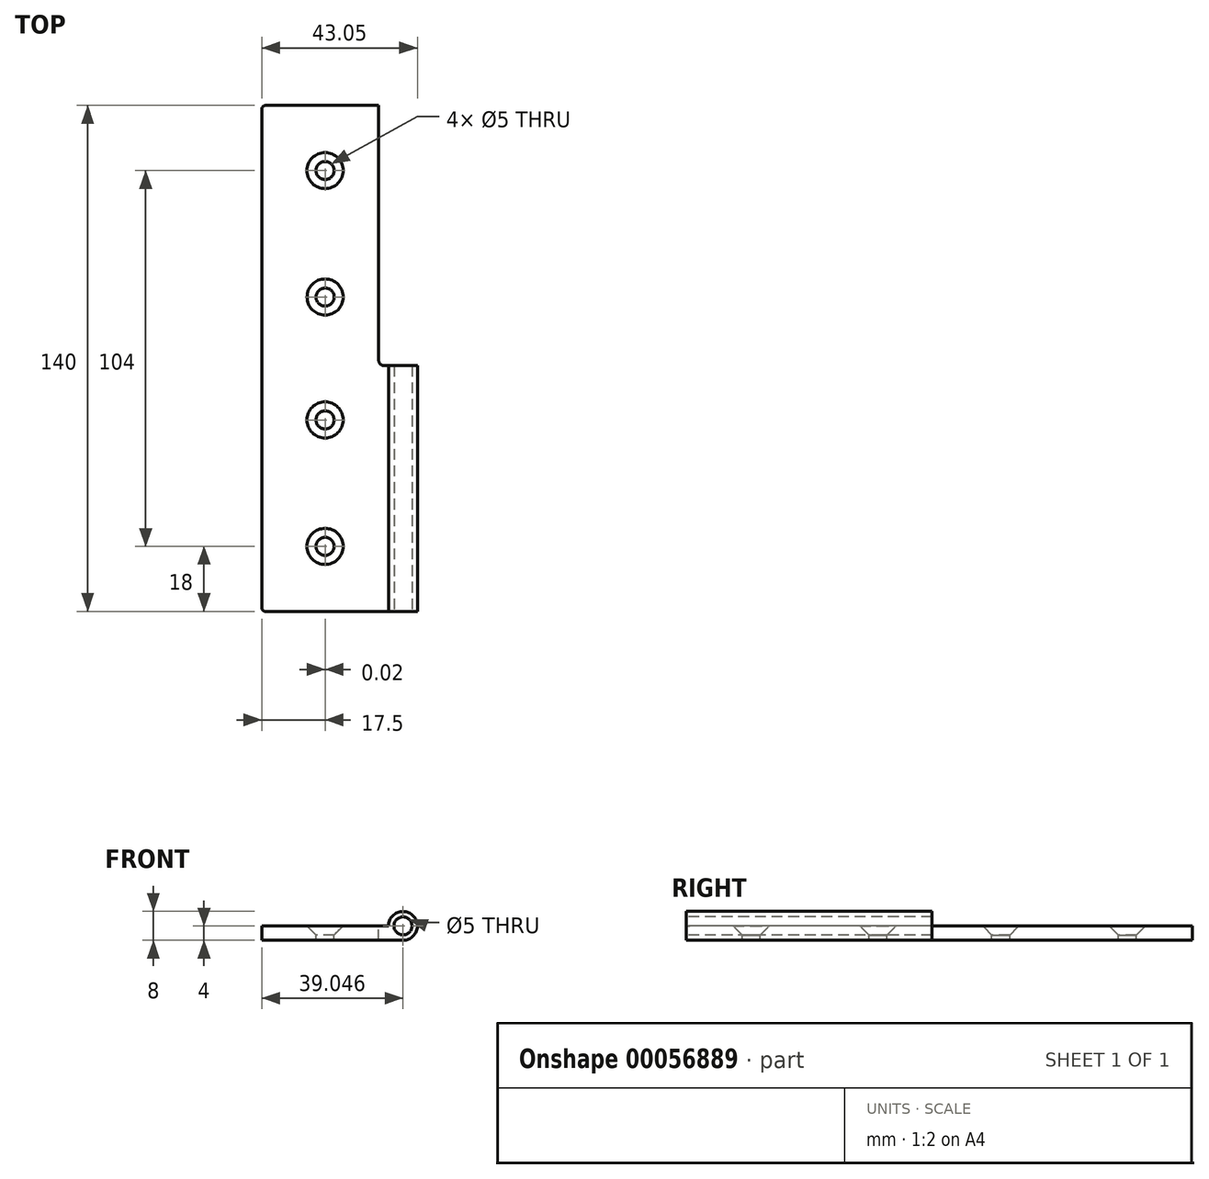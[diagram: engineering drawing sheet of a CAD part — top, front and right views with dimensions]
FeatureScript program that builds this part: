
annotation { "Feature Type Name" : "Feature", "Feature Type Description" : "" }
export const myFeature = defineFeature(function(context is Context, id is Id, definition is map)
    precondition{}
    {
        {
            var Q0;
            Q0=qCreatedBy(makeId("Top.planeOp"),FACE);
            var sketch = newSketch(context, id + "F0", { "sketchPlane" : qUnion([Q0])});
            skLineSegment(sketch, "E0.bottom", {"start": v(-17.5, 70) * mm, "end": v(17.5, 70) * mm});
            skLineSegment(sketch, "E0.top", {"start": v(-17.5, -70) * mm, "end": v(17.5, -70) * mm});
            skLineSegment(sketch, "E0.left", {"start": v(-17.5, 70) * mm, "end": v(-17.5, -70) * mm});
            skLineSegment(sketch, "E0.right", {"start": v(17.5, 70) * mm, "end": v(17.5, -70) * mm});
            skSolve(sketch);
        }
        {
            var Q0;
            Q0=makeQuery(id+"F0.imprint","IMPRINT",FACE,{"disambiguationData":[TD([[makeQuery(id+"F0.imprint","IMPRINT",EDGE,{"derivedFrom":sQuery(id+"F0.wireOp",EDGE,"E0.bottom")}),-1.0]])]});
            extrude(context, id + "F1", {"entities" : qUnion([Q0]), "depth" : 4 * mm});
        }
        {
            var Q0;
            Q0=makeQuery(id+"F1.opExtrude","SWEPT_FACE",FACE,{"disambiguationData":[OSD([sQuery(id+"F0.wireOp",EDGE,"E0.top")])]});
            var sketch = newSketch(context, id + "F2", { "sketchPlane" : qUnion([Q0])});
            skLineSegment(sketch, "E1", {"start": v(17.5, 0) * mm, "end": v(21.55, 0) * mm});
            skArc(sketch, "E2", {"start": v(21.55, 0) * mm, "mid": v(24.37, 6.83) * mm, "end": v(17.55, 4) * mm});
            skCircle(sketch, "E3", {"center": v(21.55, 4) * mm, "radius": 2.5 * mm});
            skLineSegment(sketch, "E4", {"start": v(17.5, 4) * mm, "end": v(17.55, 4) * mm});
            skSolve(sketch);
        }
        {
            var Q0;
            Q0=makeQuery(id+"F2.imprint","IMPRINT",FACE,{"disambiguationData":[TD([[makeQuery(id+"F2.imprint","IMPRINT",EDGE,{"derivedFrom":sQuery(id+"F2.wireOp",EDGE,"E2")}),1.0]])]});
            extrude(context, id + "F3", {"entities" : qUnion([Q0]), "oppositeDirection" : true, "depth" : 68 * mm});
        }
        {
            var Q0;
            Q0=makeQuery(id+"F3.opExtrude","SWEPT_BODY",BODY,{"disambiguationData":[OSD([sQuery(id+"F2.wireOp",EDGE,"E2"),sQuery(id+"F2.wireOp",EDGE,"E3")])]});
            var Q1;
            Q1=makeQuery(id+"F1.opExtrude","SWEPT_BODY",BODY,{"disambiguationData":[OSD([sQuery(id+"F0.wireOp",EDGE,"E0.bottom"),sQuery(id+"F0.wireOp",EDGE,"E0.top"),sQuery(id+"F0.wireOp",EDGE,"E0.left"),sQuery(id+"F0.wireOp",EDGE,"E0.right")])]});
            booleanBodies(context, id + "F4", {"operationType" : BooleanOperationType.UNION, "tools" : qUnion([Q0, Q1])});
        }
        {
            var Q0;
            Q0=makeQuery(id+"F4.opBoolean","MERGE",FACE,{"derivedFrom":[makeQuery(id+"F1.opExtrude","CAP_FACE",FACE,{"disambiguationData":[OSD([sQuery(id+"F0.wireOp",EDGE,"E0.bottom"),sQuery(id+"F0.wireOp",EDGE,"E0.top"),sQuery(id+"F0.wireOp",EDGE,"E0.left"),sQuery(id+"F0.wireOp",EDGE,"E0.right")])],"isStart":false}),makeQuery(id+"F3.opExtrude","SWEPT_FACE",FACE,{"disambiguationData":[OSD([sQuery(id+"F2.wireOp",EDGE,"E4")])]})]});
            var sketch = newSketch(context, id + "F5", { "sketchPlane" : qUnion([Q0])});
            skPoint(sketch, "E5", {"position": v(0, -52) * mm});
            skPoint(sketch, "E6", {"position": v(0, -17) * mm});
            skPoint(sketch, "E7", {"position": v(0.02, 17) * mm});
            skPoint(sketch, "E8", {"position": v(0, 52) * mm});
            skSolve(sketch);
        }
        {
            var Q0;
            Q0=sQuery(id+"F5.wireOp",VERTEX,"E5");
            var Q1;
            Q1=sQuery(id+"F5.wireOp",VERTEX,"E6");
            var Q2;
            Q2=sQuery(id+"F5.wireOp",VERTEX,"E7");
            var Q3;
            Q3=sQuery(id+"F5.wireOp",VERTEX,"E8");
            var Q4;
            Q4=makeQuery(id+"F3.opExtrude","SWEPT_BODY",BODY,{"disambiguationData":[OSD([sQuery(id+"F0.wireOp",EDGE,"E0.top"),sQuery(id+"F0.wireOp",EDGE,"E0.right"),sQuery(id+"F2.wireOp",EDGE,"E1"),sQuery(id+"F2.wireOp",EDGE,"E2"),sQuery(id+"F2.wireOp",EDGE,"E3"),sQuery(id+"F2.wireOp",EDGE,"E4")])]});
            hole(context, id + "F6", {"style" : HoleStyle.C_SINK, "holeDiameter" : 5 * mm, "cSinkDiameter" : 10 * mm, "endStyle" : HoleEndStyle.THROUGH, "locations" : qUnion([Q0, Q1, Q2, Q3]), "scope" : qUnion([Q4]), "cSinkAngle" : 90 * degree});
        }
        {
            var Q0;
            Q0=makeQuery(id+"F4.opBoolean","MERGE",FACE,{"derivedFrom":[makeQuery(id+"F1.opExtrude","CAP_FACE",FACE,{"disambiguationData":[OSD([sQuery(id+"F0.wireOp",EDGE,"E0.bottom"),sQuery(id+"F0.wireOp",EDGE,"E0.top"),sQuery(id+"F0.wireOp",EDGE,"E0.left"),sQuery(id+"F0.wireOp",EDGE,"E0.right")])],"isStart":false}),makeQuery(id+"F3.opExtrude","SWEPT_FACE",FACE,{"disambiguationData":[OSD([sQuery(id+"F2.wireOp",EDGE,"E4")])]})]});
            var sketch = newSketch(context, id + "F7", { "sketchPlane" : qUnion([Q0])});
            skLineSegment(sketch, "E9", {"start": v(14.82, 70) * mm, "end": v(14.82, -0.5) * mm});
            skLineSegment(sketch, "E10", {"start": v(17.55, -2) * mm, "end": v(16.32, -2) * mm});
            skArc(sketch, "E11.filletArc", {"start": v(14.82, -0.5) * mm, "mid": v(15.26, -1.56) * mm, "end": v(16.32, -2) * mm});
            skLineSegment(sketch, "E12", {"start": v(14.82, 70) * mm, "end": v(17.55, 70) * mm});
            skLineSegment(sketch, "E13", {"start": v(17.55, -2) * mm, "end": v(17.55, 70) * mm});
            skSolve(sketch);
        }
        {
            var Q0;
            {var subQ4=sQuery(id+"F7.wireOp",EDGE,"E9");Q0=makeQuery(id+"F7.imprint","IMPRINT",FACE,{"disambiguationData":[TD([[makeQuery(id+"F7.imprint","IMPRINT",EDGE,{"derivedFrom":subQ4}),1.0]])]});}
            extrude(context, id + "F8", {"entities" : qUnion([Q0]), "operationType" : NewBodyOperationType.REMOVE, "endBound" : BoundingType.THROUGH_ALL, "oppositeDirection" : true, "depth" : 25 * mm});
        }
        {
            var Q0;
            Q0=makeQuery(id+"F1.opExtrude","SWEPT_EDGE",EDGE,{"disambiguationData":[OSD([sQuery(id+"F0.wireOp",EDGE,"E0.top"),sQuery(id+"F0.wireOp",EDGE,"E0.left")])]});
            var Q1;
            Q1=makeQuery(id+"F1.opExtrude","SWEPT_EDGE",EDGE,{"disambiguationData":[OSD([sQuery(id+"F0.wireOp",EDGE,"E0.bottom"),sQuery(id+"F0.wireOp",EDGE,"E0.left")])]});
            var Q2;
            Q2=makeQuery(id+"F8.boolean.opBoolean","COPY",EDGE,{"derivedFrom":makeQuery(id+"F8.opExtrude","SWEPT_EDGE",EDGE,{"disambiguationData":[OSD([sQuery(id+"F0.wireOp",EDGE,"E0.bottom"),sQuery(id+"F7.wireOp",EDGE,"E9"),sQuery(id+"F7.wireOp",EDGE,"E12")])]})});
            fillet(context, id + "F9", {"entities" : qUnion([Q0, Q1, Q2]), "radius" : 1 * mm, "tangentPropagation" : true, "allowEdgeOverflow" : false});
        }
    });
